# Revit family: RRTNT3041_2
name_source: partatom
category: Generic Models
revit_build: Autodesk Revit 2018 (Build: 20190510_1515(x64)
units: mm (PartAtom-declared; Revit-internal decimal feet)

## family parameters
Always vertical = No
Can host rebar = No
Cut with Voids When Loaded = No
Part Type = Normal
Room Calculation Point = No
Round Connector Dimension = Use Diameter
Shared = Yes
Work Plane-Based = Yes

## types (6) — shared parameters
Default Elevation = 48 "
Patent Information = D653,524
Rack Material = <By Category>

## per-type parameters (varying)
| type | 1 Slot | 2 Slots | 3 Slots | 4 Slots | Ctlr Slot 3 Length | Ctrl Slot 2 Length | Ctrl Slot 4 Length | Description | Offset 2 | Offset 3 | Offset 4 | Rack Length | Slot 1 Length | Slot 2 Length | Slot 2 Offset | Slot 3 Length | Slot 3 Offset | Slot 4 Length | Slot 4 Offset |
| RRTNT304121/2 | Yes | No | No | No | 8.25 " | 8.125 " | 8.375 " | Tented Rack 304 12 Inch long 1/2 Inch Mounting Hardware | 2 " | 2 " | 2 " | 12 " | 8 " | 8 " | 8.5 " | 8 " | 18.66 " | 8 " | 26.75 " |
| RRTNT304181/2 | No | Yes | No | No | 6.75 " | 6.5 " | 6.875 " | Tented Rack 304 18 Inch long 1/2 Inch Mounting Hardware | 9.5 " | 2 " | 2 " | 18 " | 6.5 " | 6.5 " | 9.5 " | 6.5 " | 18.66 " | 6.5 " | 26.75 " |
| RRTNT304241/2 | No | Yes | No | No | 9.75 " | 9.5 " | 9.875 " | Tented Rack 304 24 Inch long 1/2 Inch Mounting Hardware | 12.5 " | 2 " | 2 " | 24 " | 9.5 " | 9.5 " | 12.5 " | 9.5 " | 18.66 " | 9.5 " | 26.75 " |
| RRTNT304301/2 | No | No | Yes | No | 8 " | 8 " | 8.375 " | Tented Rack 304 30 Inch long 1/2 Inch Mounting Hardware | 11 " | 20 " | 2 " | 30 " | 8 " | 8 " | 11 " | 8 " | 20 " | 8 " | 26.75 " |
| RRTNT304361/2 | No | No | No | Yes | 7.25 " | 7.25 " | 7.25 " | Tented Rack 304 36 Inch long 1/2 Inch Mounting Hardware | 10.25 " | 18.5 " | 26.75 " | 36 " | 7.25 " | 7.25 " | 10.25 " | 7.25 " | 18.5 " | 7.25 " | 26.75 " |
| RRTNT304481/2 | No | No | No | Yes | 10.25 " | 10.25 " | 10.25 " | Tented Rack 304 48 Inch long 1/2 Inch Mounting Hardware | 13.25 " | 24.5 " | 35.75 " | 48 " | 10.25 " | 10.25 " | 13.25 " | 10.25 " | 24.5 " | 10.25 " | 35.75 " |

note: column(s) folded — value = type name in every type: Catalog Number

## geometry (parser evidence)
native form markers: Sweep x6
no freeform markers — native parametric forms only
